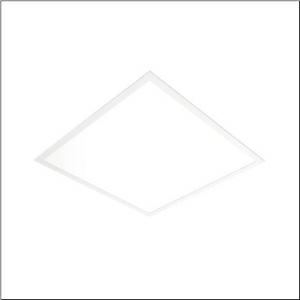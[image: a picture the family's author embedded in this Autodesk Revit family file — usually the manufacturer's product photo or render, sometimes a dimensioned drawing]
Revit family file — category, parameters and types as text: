
# Revit family: apollon_r__41_51mh11wm2443_3aa7
name_source: partatom
category: Lighting Fixtures
units: mm (PartAtom-declared; Revit-internal decimal feet)

## family parameters
Cut with Voids When Loaded = No
Host = Face
Light Source = No
Part Type = Normal
Room Calculation Point = No
Round Connector Dimension = Use Diameter
Shared = No

## types (1)
- --- (1 x LED, 4380 lm, 35 W, 4000K)
    Apparent Load = 35 VA
    CIE Flux Codes = 61 87 97 100 100
    Color Rendering = 80
    Color Temperature = 4000K
    Default Elevation = 1800 mm
    Description = Apollon® 41, office luminaire, primary optical cover: prismatic diffuser, of PS, light emission: direct distribution, primary light characteristic: symmetric, installation type: lay-in mounting, LED, rated luminous flux: 4.375lm, luminous efficacy: 125lm/W, light colour: 840, colour temperature: 4000K, control gear: ON/OFF Multilumen, with terminal, 3-pole, mains connection: 220..240V, AC, 50/60Hz, rated input power: 35W, housing, of aluminium section, traffic white (RAL 9016), module: M625, length: 620mm, width: 620mm, height: 60mm, recess depth: 180mm, housing upper side, of sheet steel, protection rating (complete): IP20, protection rating (lamp compartment, on room side): IP40, insulation class (complete): insulation class II (safety insulation), certification: CE, ENEC, impact resistance: IK03, permissible operating ambient temperature: -25..+40°C, packaging unit: 1 piece
    Height = 0 mm  [stored 0 ft]
    Lamp = 1 x LED
    Lamp Light Flux = 4380 lm
    Lamp Power = 35 W
    Lamp count = 1
    Length = 620 mm
    Luminous efficacy = 125 lm/W
    Manufacturer = Siteco
    ModVariant = No
    Model = 51MH11WM2443
    Mounting Place = Ceiling
    Mounting Type = Recessed
    Number of Poles = 1
    OnlyDefault = Yes
    Power Factor = 1
    Product Name = Apollon® 41
    Product group = office luminaire | ceiling recessed
    ProductGroupID = 400
    Protection Class = Protection class II
    Protection Degree = IP 20
    RLX_Detail_Level = 1
    RLX_Emergency_Light_Flux = 0 lm
    RLX_Emergency_Type = 0
    RLX_Emergency_Type_DB = No
    RlxData = <blob elided: 12993 chars, md5=35605d9f>
    Socket = socket
    Standby Power = 0 W
    System Light Flux = 4380 lm
    System Power = 35 W
    Type Comments = factory setting: luminous flux: 100 % | (ON | ON) | 900 mA
    Type Image = l_1291024.jpg
    URL = http://relux.com
    VarID = @adj_010421
    Voltage = 0 V
    Weight = 0.00 kg
    Width = 620 mm

note: [stored X ft] marks values corroborated as IEEE doubles in the binary element streams (Revit-internal decimal feet)

## geometry (parser evidence)
native form markers: Sweep x11
no freeform markers — native parametric forms only
